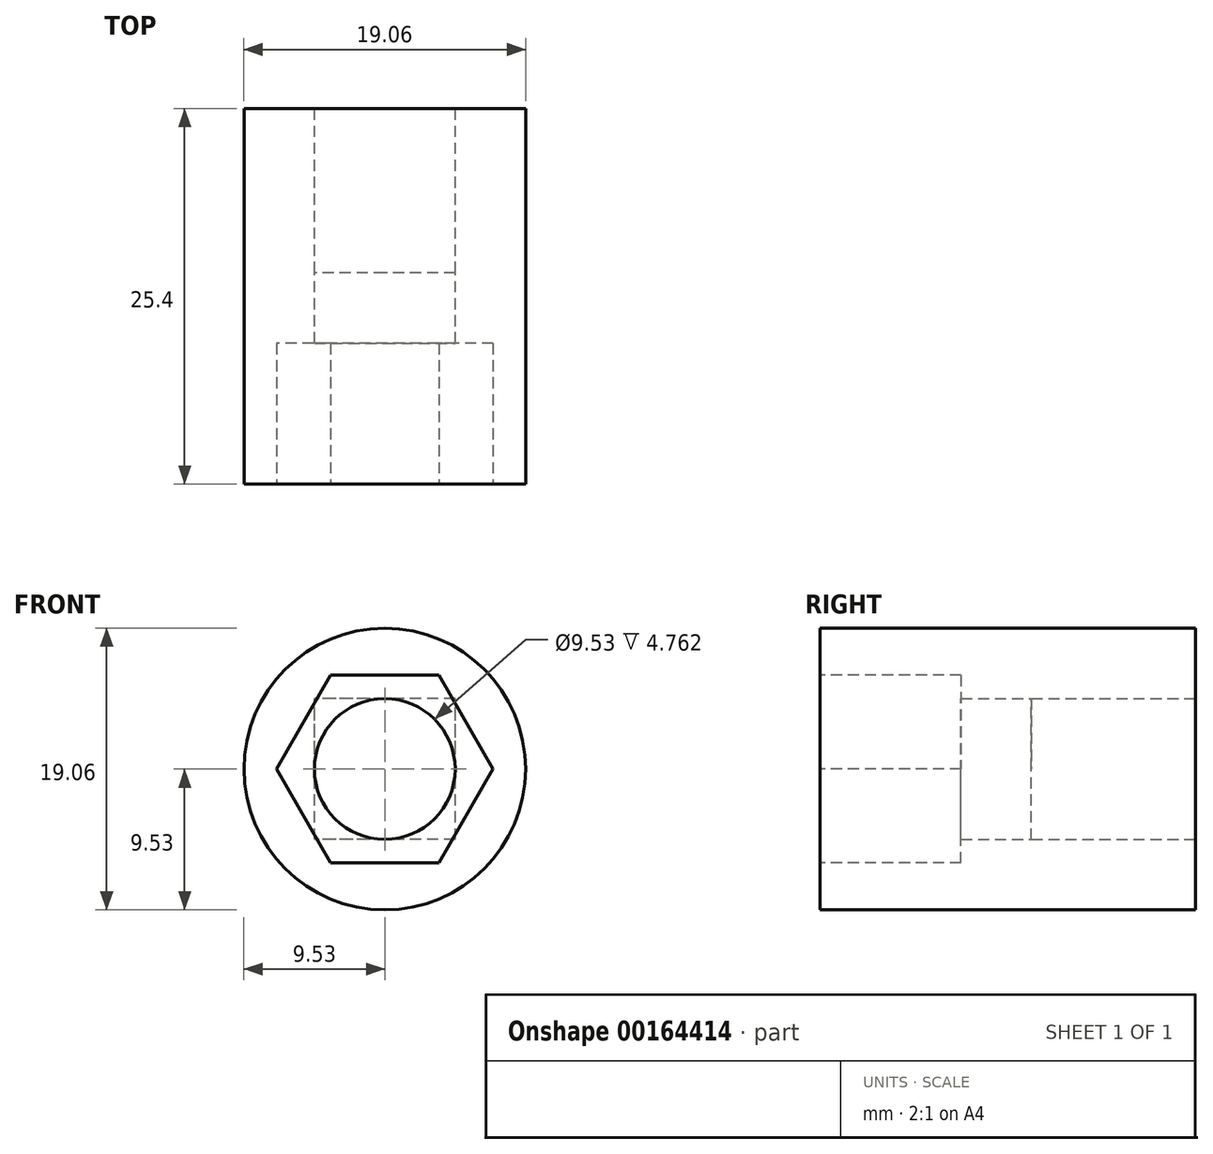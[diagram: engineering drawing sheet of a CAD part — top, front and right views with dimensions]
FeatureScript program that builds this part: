
annotation { "Feature Type Name" : "Feature", "Feature Type Description" : "" }
export const myFeature = defineFeature(function(context is Context, id is Id, definition is map)
    precondition{}
    {
        {
            var Q0;
            Q0=qCreatedBy(makeId("Front.planeOp"),FACE);
            var sketch = newSketch(context, id + "F0", { "sketchPlane" : qUnion([Q0])});
            skCircle(sketch, "E0", {"center": v(0, 0) * mm, "radius": 9.53 * mm});
            skSolve(sketch);
        }
        {
            var Q0;
            Q0 = qSketchRegion(id + "F0", true);
            extrude(context, id + "F1", {"entities" : qUnion([Q0]), "oppositeDirection" : true, "depth" : 25.4 * mm});
        }
        {
            var Q0;
            Q0=makeQuery(id+"F1.opExtrude","CAP_FACE",FACE,{"disambiguationData":[OSD([sQuery(id+"F0.wireOp",EDGE,"E0")])],"isStart":false});
            var sketch = newSketch(context, id + "F2", { "sketchPlane" : qUnion([Q0])});
            skLineSegment(sketch, "E1.bottom", {"start": v(-4.76, -4.76) * mm, "end": v(4.76, -4.76) * mm});
            skLineSegment(sketch, "E1.top", {"start": v(-4.76, 4.76) * mm, "end": v(4.76, 4.76) * mm});
            skLineSegment(sketch, "E1.left", {"start": v(-4.76, -4.76) * mm, "end": v(-4.76, 4.76) * mm});
            skLineSegment(sketch, "E1.right", {"start": v(4.76, -4.76) * mm, "end": v(4.76, 4.76) * mm});
            skPoint(sketch, "E1.middle", {"position": v(0, 0) * mm});
            skCircle(sketch, "E2", {"center": v(0, 0) * mm, "radius": 4.76 * mm});
            skSolve(sketch);
        }
        {
            var Q0;
            {var subQ0=sQuery(id+"F2.wireOp",EDGE,"E2");var subQ1=makeQuery(id+"F2.imprint","INTERSECT",VERTEX,{"derivedFrom":[sQuery(id+"F2.wireOp",EDGE,"E1.top"),subQ0]});Q0=makeQuery(id+"F2.imprint","IMPRINT",FACE,{"disambiguationData":[TD([[makeQuery(id+"F2.imprint","IMPRINT",EDGE,{"disambiguationData":[TD([[subQ1,1.0]])],"derivedFrom":subQ0}),1.0]])]});}
            extrude(context, id + "F3", {"entities" : qUnion([Q0]), "operationType" : NewBodyOperationType.REMOVE, "endBound" : BoundingType.THROUGH_ALL, "oppositeDirection" : true, "depth" : 25.4 * mm});
        }
        {
            var Q0;
            Q0 = qSketchRegion(id + "F2", true);
            extrude(context, id + "F4", {"entities" : qUnion([Q0]), "operationType" : NewBodyOperationType.REMOVE, "oppositeDirection" : true, "depth" : 11.1 * mm});
        }
        {
            var Q0;
            Q0=makeQuery(id+"F1.opExtrude","CAP_FACE",FACE,{"disambiguationData":[OSD([sQuery(id+"F0.wireOp",EDGE,"E0")])],"isStart":true});
            var sketch = newSketch(context, id + "F5", { "sketchPlane" : qUnion([Q0])});
            skCircle(sketch, "E3.cCircle", {"center": v(0, 0) * mm, "radius": 6.35 * mm, "construction": true});
            skLineSegment(sketch, "E3.0", {"start": v(-3.67, -6.35) * mm, "end": v(-7.33, 0) * mm});
            skLineSegment(sketch, "E3.1", {"start": v(-7.33, 0) * mm, "end": v(-3.67, 6.35) * mm});
            skLineSegment(sketch, "E3.2", {"start": v(-3.67, 6.35) * mm, "end": v(3.67, 6.35) * mm});
            skLineSegment(sketch, "E3.3", {"start": v(3.67, 6.35) * mm, "end": v(7.33, 0) * mm});
            skLineSegment(sketch, "E3.4", {"start": v(7.33, 0) * mm, "end": v(3.67, -6.35) * mm});
            skLineSegment(sketch, "E3.5", {"start": v(3.67, -6.35) * mm, "end": v(-3.67, -6.35) * mm});
            skPoint(sketch, "E3.0.midPoint", {"position": v(-5.5, -3.18) * mm});
            skSolve(sketch);
        }
        {
            var Q0;
            Q0 = qSketchRegion(id + "F5", true);
            extrude(context, id + "F6", {"entities" : qUnion([Q0]), "operationType" : NewBodyOperationType.REMOVE, "oppositeDirection" : true, "depth" : 9.52 * mm});
        }
    });
